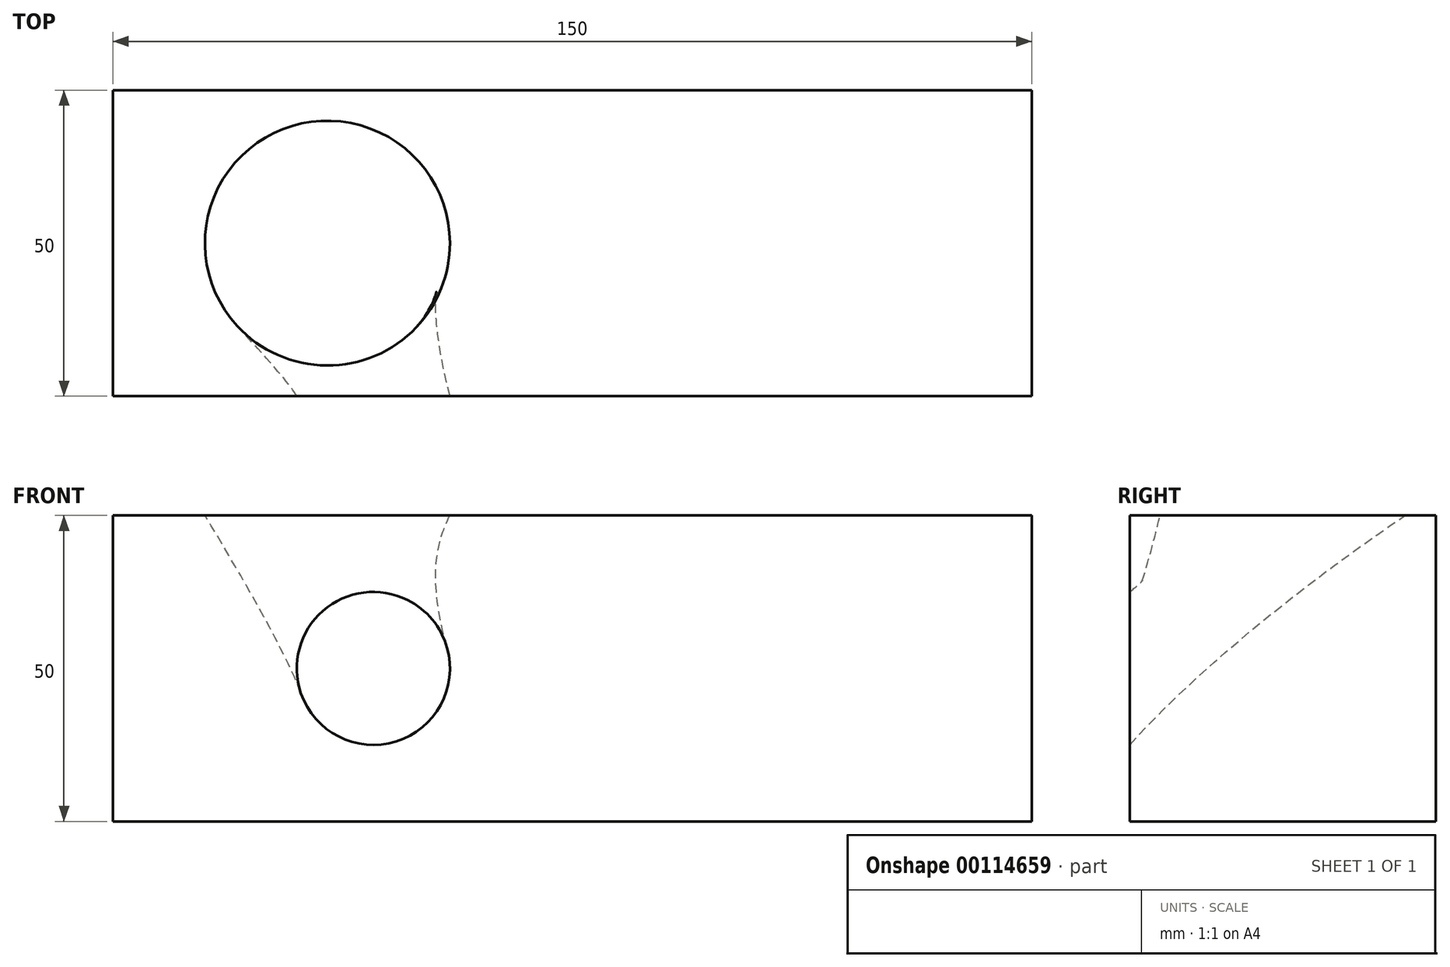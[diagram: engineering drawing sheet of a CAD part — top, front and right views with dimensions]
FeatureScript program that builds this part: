
annotation { "Feature Type Name" : "Feature", "Feature Type Description" : "" }
export const myFeature = defineFeature(function(context is Context, id is Id, definition is map)
    precondition{}
    {
        {
            var Q0;
            Q0=qCreatedBy(makeId("Front.planeOp"),FACE);
            var sketch = newSketch(context, id + "F0", { "sketchPlane" : qUnion([Q0])});
            skLineSegment(sketch, "E0.bottom", {"start": v(-75, 25) * mm, "end": v(75, 25) * mm});
            skLineSegment(sketch, "E0.top", {"start": v(-75, -25) * mm, "end": v(75, -25) * mm});
            skLineSegment(sketch, "E0.left", {"start": v(-75, 25) * mm, "end": v(-75, -25) * mm});
            skLineSegment(sketch, "E0.right", {"start": v(75, 25) * mm, "end": v(75, -25) * mm});
            skPoint(sketch, "E0.middle", {"position": v(0, 0) * mm});
            skSolve(sketch);
        }
        {
            var Q0;
            Q0 = qSketchRegion(id + "F0", true);
            extrude(context, id + "F1", {"entities" : qUnion([Q0]), "depth" : 50 * mm, "symmetric" : true});
        }
        {
            var Q0;
            Q0=makeQuery(id+"F1.opExtrude","SWEPT_FACE",FACE,{"disambiguationData":[OSD([sQuery(id+"F0.wireOp",EDGE,"E0.bottom")])]});
            var sketch = newSketch(context, id + "F2", { "sketchPlane" : qUnion([Q0])});
            skCircle(sketch, "E1", {"center": v(-40, 0) * mm, "radius": 20 * mm});
            skSolve(sketch);
        }
        {
            var Q0;
            Q0=makeQuery(id+"F1.opExtrude","CAP_FACE",FACE,{"disambiguationData":[OSD([sQuery(id+"F0.wireOp",EDGE,"E0.bottom"),sQuery(id+"F0.wireOp",EDGE,"E0.top"),sQuery(id+"F0.wireOp",EDGE,"E0.left"),sQuery(id+"F0.wireOp",EDGE,"E0.right")])],"isStart":false});
            var sketch = newSketch(context, id + "F3", { "sketchPlane" : qUnion([Q0])});
            skCircle(sketch, "E2", {"center": v(-32.5, 0) * mm, "radius": 12.5 * mm});
            skSolve(sketch);
        }
        {
            var Q1;
            Q1=makeQuery(id+"F2.imprint","IMPRINT",FACE,{"disambiguationData":[TD([[makeQuery(id+"F2.imprint","IMPRINT",EDGE,{"derivedFrom":sQuery(id+"F2.wireOp",EDGE,"E1")}),1.0]])]});
            var Q2;
            Q2=makeQuery(id+"F3.imprint","IMPRINT",FACE,{"disambiguationData":[TD([[makeQuery(id+"F3.imprint","IMPRINT",EDGE,{"derivedFrom":sQuery(id+"F3.wireOp",EDGE,"E2")}),1.0]])]});
            loft(context, id + "F4", {"operationType" : NewBodyOperationType.REMOVE, "sheetProfilesArray" : [{ "sheetProfileEntities" : qUnion([Q1]) }, { "sheetProfileEntities" : qUnion([Q2]) }]});
        }
    });
